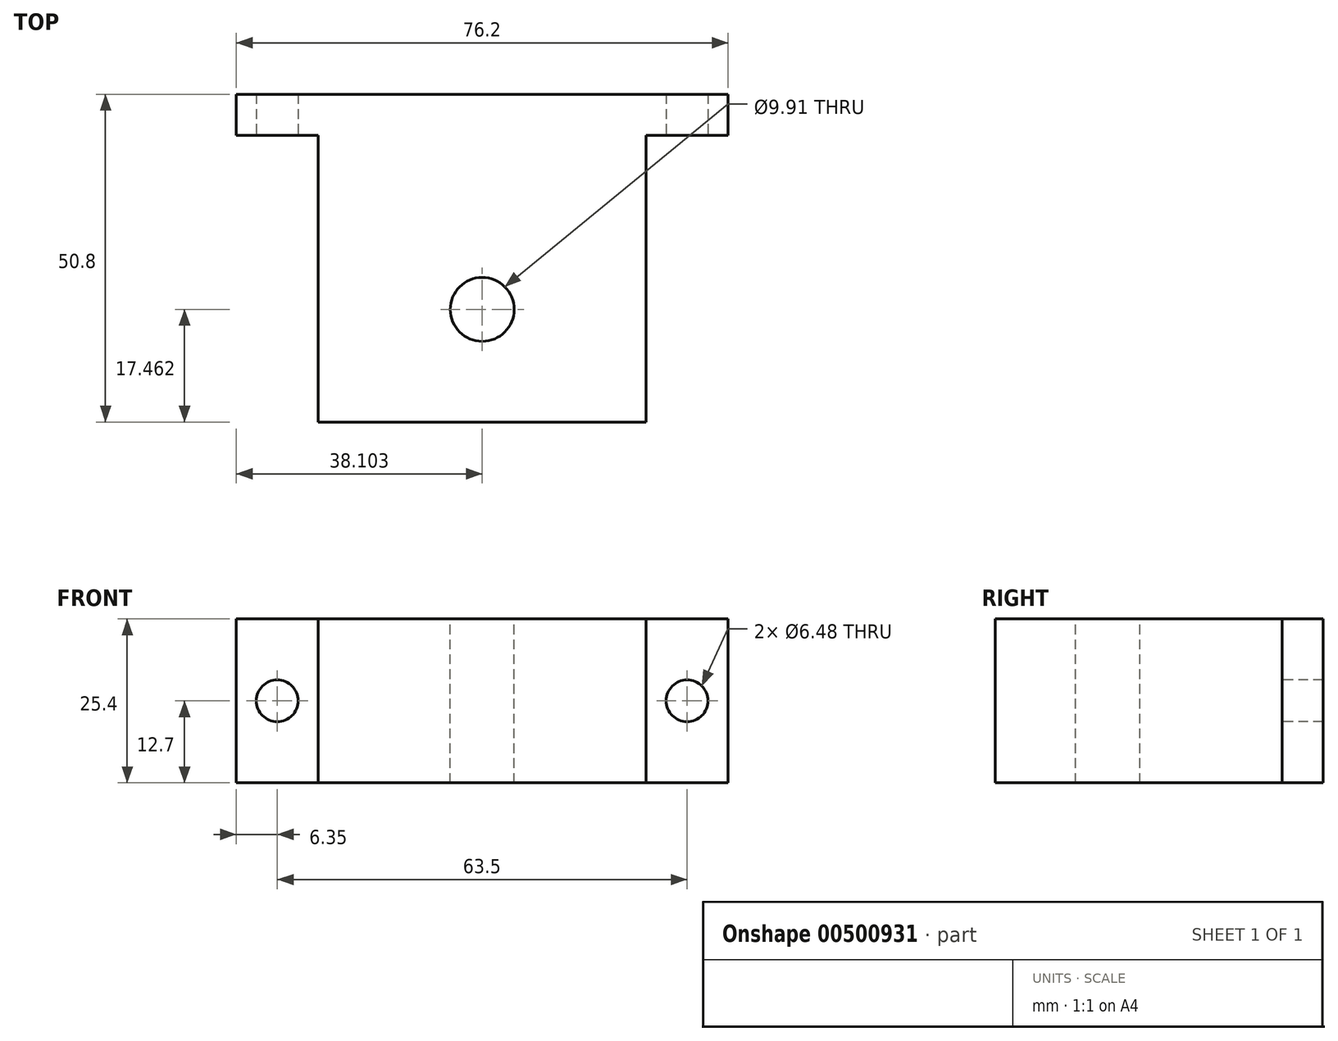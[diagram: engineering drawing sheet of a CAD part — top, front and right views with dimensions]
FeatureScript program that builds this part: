
annotation { "Feature Type Name" : "Feature", "Feature Type Description" : "" }
export const myFeature = defineFeature(function(context is Context, id is Id, definition is map)
    precondition{}
    {
        {
            var Q0;
            Q0=qCreatedBy(makeId("Top.planeOp"),FACE);
            var sketch = newSketch(context, id + "F0", { "sketchPlane" : qUnion([Q0])});
            skLineSegment(sketch, "E0", {"start": v(0, 0) * mm, "end": v(76.2, 0) * mm});
            skLineSegment(sketch, "E1", {"start": v(76.2, 0) * mm, "end": v(76.2, -6.35) * mm});
            skLineSegment(sketch, "E2", {"start": v(76.2, -6.35) * mm, "end": v(63.5, -6.35) * mm});
            skLineSegment(sketch, "E3", {"start": v(63.5, -6.35) * mm, "end": v(63.5, -50.8) * mm});
            skLineSegment(sketch, "E4", {"start": v(63.5, -50.8) * mm, "end": v(12.7, -50.8) * mm});
            skLineSegment(sketch, "E5", {"start": v(12.7, -50.8) * mm, "end": v(12.7, -6.35) * mm});
            skLineSegment(sketch, "E6", {"start": v(12.7, -6.35) * mm, "end": v(0, -6.35) * mm});
            skLineSegment(sketch, "E7", {"start": v(0, -6.35) * mm, "end": v(0, 0) * mm});
            skSolve(sketch);
        }
        {
            var Q0;
            Q0=makeQuery(id+"F0.imprint","IMPRINT",FACE,{"disambiguationData":[TD([[makeQuery(id+"F0.imprint","IMPRINT",EDGE,{"derivedFrom":sQuery(id+"F0.wireOp",EDGE,"E0")}),-1.0]])]});
            extrude(context, id + "F1", {"entities" : qUnion([Q0]), "depth" : 25.4 * mm, "offsetDistance" : 25.4 * mm});
        }
        {
            var Q0;
            Q0=makeQuery(id+"F1.opExtrude","SWEPT_FACE",FACE,{"disambiguationData":[OSD([sQuery(id+"F0.wireOp",EDGE,"E2")])]});
            var sketch = newSketch(context, id + "F2", { "sketchPlane" : qUnion([Q0])});
            skSolve(sketch);
        }
        {
            var Q0;
            {var subQ0=sQuery(id+"F0.wireOp",EDGE,"E2");Q0=makeQuery(id+"F2.imprint","IMPRINT",FACE,{"disambiguationData":[TD([[makeQuery(id+"F2.imprint","IMPRINT",EDGE,{"derivedFrom":makeQuery(id+"F1.opExtrude","CAP_EDGE",EDGE,{"disambiguationData":[OSD([subQ0])],"isStart":true})}),-1.0]])]});}
            var sketch = newSketch(context, id + "F3", { "sketchPlane" : qUnion([Q0])});
            skCircle(sketch, "E8", {"center": v(69.85, 12.7) * mm, "radius": 3.24 * mm});
            skSolve(sketch);
        }
        {
            var Q0;
            Q0=makeQuery(id+"F1.opExtrude","SWEPT_FACE",FACE,{"disambiguationData":[OSD([sQuery(id+"F0.wireOp",EDGE,"E6")])]});
            var sketch = newSketch(context, id + "F4", { "sketchPlane" : qUnion([Q0])});
            skCircle(sketch, "E9", {"center": v(6.35, 12.7) * mm, "radius": 3.24 * mm});
            skPoint(sketch, "E9.centerSnap0", {"position": v(0, 12.7) * mm});
            skSolve(sketch);
        }
        {
            var Q0;
            Q0=makeQuery(id+"F4.imprint","IMPRINT",FACE,{"disambiguationData":[TD([[makeQuery(id+"F4.imprint","IMPRINT",EDGE,{"derivedFrom":sQuery(id+"F4.wireOp",EDGE,"E9")}),1.0]])]});
            extrude(context, id + "F5", {"entities" : qUnion([Q0]), "operationType" : NewBodyOperationType.REMOVE, "oppositeDirection" : true, "depth" : 25.4 * mm, "offsetDistance" : 25.4 * mm});
        }
        {
            var Q0;
            Q0=makeQuery(id+"F3.imprint","IMPRINT",FACE,{"disambiguationData":[TD([[makeQuery(id+"F3.imprint","IMPRINT",EDGE,{"derivedFrom":sQuery(id+"F3.wireOp",EDGE,"E8")}),1.0]])]});
            extrude(context, id + "F6", {"entities" : qUnion([Q0]), "operationType" : NewBodyOperationType.REMOVE, "oppositeDirection" : true, "depth" : 25.4 * mm, "offsetDistance" : 25.4 * mm});
        }
        {
            var Q0;
            Q0=makeQuery(id+"F1.opExtrude","CAP_FACE",FACE,{"disambiguationData":[OSD([sQuery(id+"F0.wireOp",EDGE,"E0"),sQuery(id+"F0.wireOp",EDGE,"E1"),sQuery(id+"F0.wireOp",EDGE,"E2"),sQuery(id+"F0.wireOp",EDGE,"E3"),sQuery(id+"F0.wireOp",EDGE,"E4"),sQuery(id+"F0.wireOp",EDGE,"E5"),sQuery(id+"F0.wireOp",EDGE,"E6"),sQuery(id+"F0.wireOp",EDGE,"E7")])],"isStart":false});
            var sketch = newSketch(context, id + "F7", { "sketchPlane" : qUnion([Q0])});
            skCircle(sketch, "E10", {"center": v(38.1, -33.34) * mm, "radius": 4.95 * mm});
            skSolve(sketch);
        }
        {
            var Q0;
            Q0=makeQuery(id+"F7.imprint","IMPRINT",FACE,{"disambiguationData":[TD([[makeQuery(id+"F7.imprint","IMPRINT",EDGE,{"derivedFrom":sQuery(id+"F7.wireOp",EDGE,"E10")}),1.0]])]});
            extrude(context, id + "F8", {"entities" : qUnion([Q0]), "operationType" : NewBodyOperationType.REMOVE, "oppositeDirection" : true, "depth" : 25.4 * mm, "offsetDistance" : 25.4 * mm});
        }
    });
